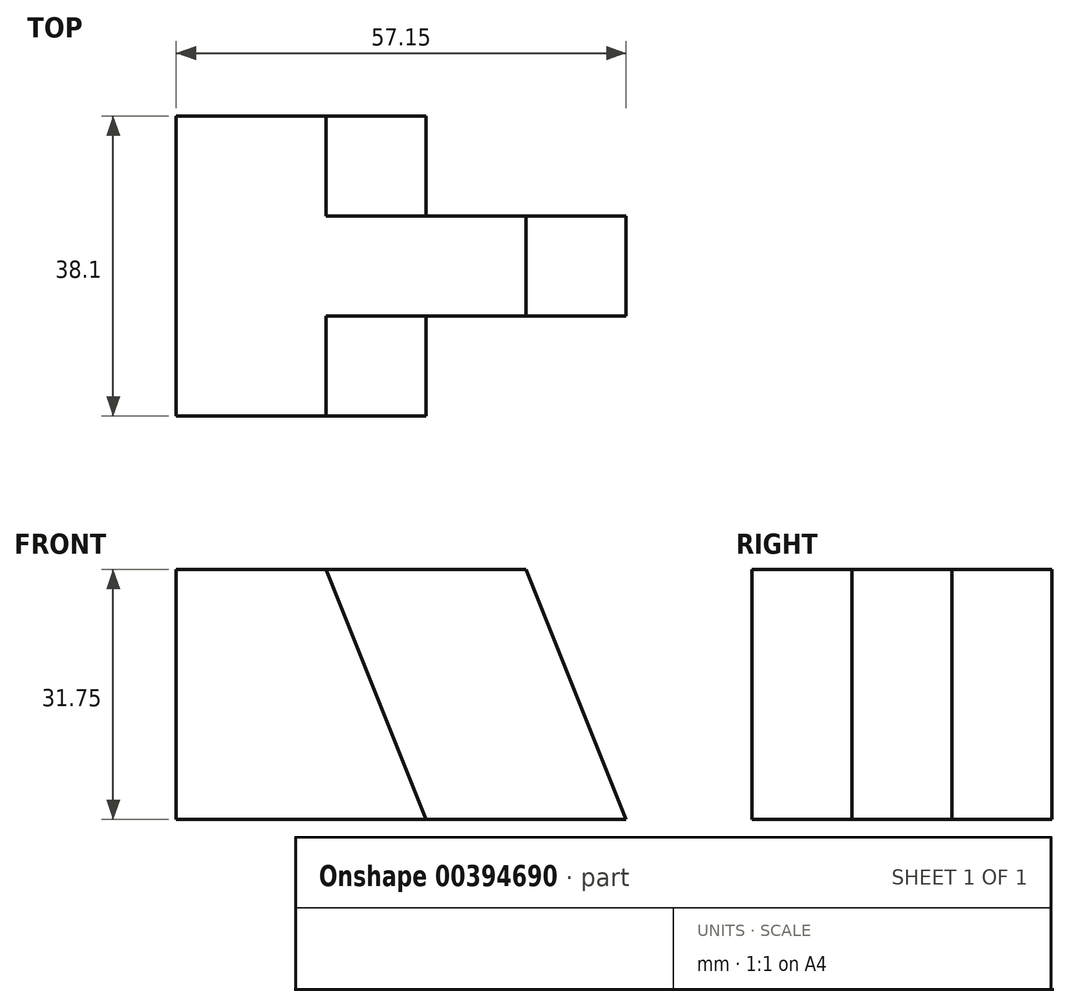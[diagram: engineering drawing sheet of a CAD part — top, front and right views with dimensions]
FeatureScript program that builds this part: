
annotation { "Feature Type Name" : "Feature", "Feature Type Description" : "" }
export const myFeature = defineFeature(function(context is Context, id is Id, definition is map)
    precondition{}
    {
        {
            var Q0;
            Q0=qCreatedBy(makeId("Front.planeOp"),FACE);
            var sketch = newSketch(context, id + "F0", { "sketchPlane" : qUnion([Q0])});
            skLineSegment(sketch, "E0", {"start": v(0, 0) * mm, "end": v(0, 31.75) * mm});
            skLineSegment(sketch, "E1", {"start": v(0, 31.75) * mm, "end": v(19.05, 31.75) * mm});
            skLineSegment(sketch, "E2", {"start": v(0, 0) * mm, "end": v(31.75, 0) * mm});
            skLineSegment(sketch, "E3", {"start": v(31.75, 0) * mm, "end": v(19.05, 31.75) * mm});
            skLineSegment(sketch, "E4", {"start": v(31.75, 0) * mm, "end": v(57.15, 0) * mm});
            skLineSegment(sketch, "E5", {"start": v(19.05, 31.75) * mm, "end": v(44.45, 31.75) * mm});
            skLineSegment(sketch, "E6", {"start": v(44.45, 31.75) * mm, "end": v(57.15, 0) * mm});
            skSolve(sketch);
        }
        {
            var Q0;
            Q0 = qSketchRegion(id + "F0", true);
            extrude(context, id + "F1", {"entities" : qUnion([Q0]), "depth" : 38.1 * mm});
        }
        {
            var Q0;
            Q0=makeQuery(id+"F1.opExtrude","CAP_FACE",FACE,{"disambiguationData":[OSD([sQuery(id+"F0.wireOp",EDGE,"E0"),sQuery(id+"F0.wireOp",EDGE,"E1"),sQuery(id+"F0.wireOp",EDGE,"E2"),sQuery(id+"F0.wireOp",EDGE,"E4"),sQuery(id+"F0.wireOp",EDGE,"E5"),sQuery(id+"F0.wireOp",EDGE,"E6")])],"isStart":false});
            var sketch = newSketch(context, id + "F2", { "sketchPlane" : qUnion([Q0])});
            skLineSegment(sketch, "E7", {"start": v(0, 31.75) * mm, "end": v(19.05, 31.75) * mm});
            skLineSegment(sketch, "E8", {"start": v(0, 0) * mm, "end": v(31.75, 0) * mm});
            skLineSegment(sketch, "E9", {"start": v(19.05, 31.75) * mm, "end": v(31.75, 0) * mm});
            skSolve(sketch);
        }
        {
            var Q0;
            Q0 = qSketchRegion(id + "F2", true);
            var Q1;
            {var subQ0=sQuery(id+"F2.wireOp",EDGE,"E9");Q1=makeQuery(id+"F2.imprint","IMPRINT",FACE,{"disambiguationData":[TD([[makeQuery(id+"F2.imprint","IMPRINT",EDGE,{"derivedFrom":subQ0}),1.0]])]});}
            extrude(context, id + "F3", {"entities" : qUnion([Q0, Q1]), "operationType" : NewBodyOperationType.REMOVE, "oppositeDirection" : true, "depth" : 12.7 * mm});
        }
        {
            var Q0;
            Q0=makeQuery(id+"F1.opExtrude","CAP_FACE",FACE,{"disambiguationData":[OSD([sQuery(id+"F0.wireOp",EDGE,"E0"),sQuery(id+"F0.wireOp",EDGE,"E1"),sQuery(id+"F0.wireOp",EDGE,"E2"),sQuery(id+"F0.wireOp",EDGE,"E4"),sQuery(id+"F0.wireOp",EDGE,"E5"),sQuery(id+"F0.wireOp",EDGE,"E6")])],"isStart":true});
            var sketch = newSketch(context, id + "F4", { "sketchPlane" : qUnion([Q0])});
            skLineSegment(sketch, "E10", {"start": v(0, 31.75) * mm, "end": v(-19.05, 31.75) * mm});
            skLineSegment(sketch, "E11", {"start": v(0, 0) * mm, "end": v(-31.75, 0) * mm});
            skLineSegment(sketch, "E12", {"start": v(-31.75, 0) * mm, "end": v(-19.05, 31.75) * mm});
            skSolve(sketch);
        }
        {
            var Q0;
            Q0 = qSketchRegion(id + "F4", true);
            var Q1;
            {var subQ0=sQuery(id+"F4.wireOp",EDGE,"E12");Q1=makeQuery(id+"F4.imprint","IMPRINT",FACE,{"disambiguationData":[TD([[makeQuery(id+"F4.imprint","IMPRINT",EDGE,{"derivedFrom":subQ0}),1.0]])]});}
            extrude(context, id + "F5", {"entities" : qUnion([Q0, Q1]), "operationType" : NewBodyOperationType.REMOVE, "oppositeDirection" : true, "depth" : 12.7 * mm});
        }
    });
